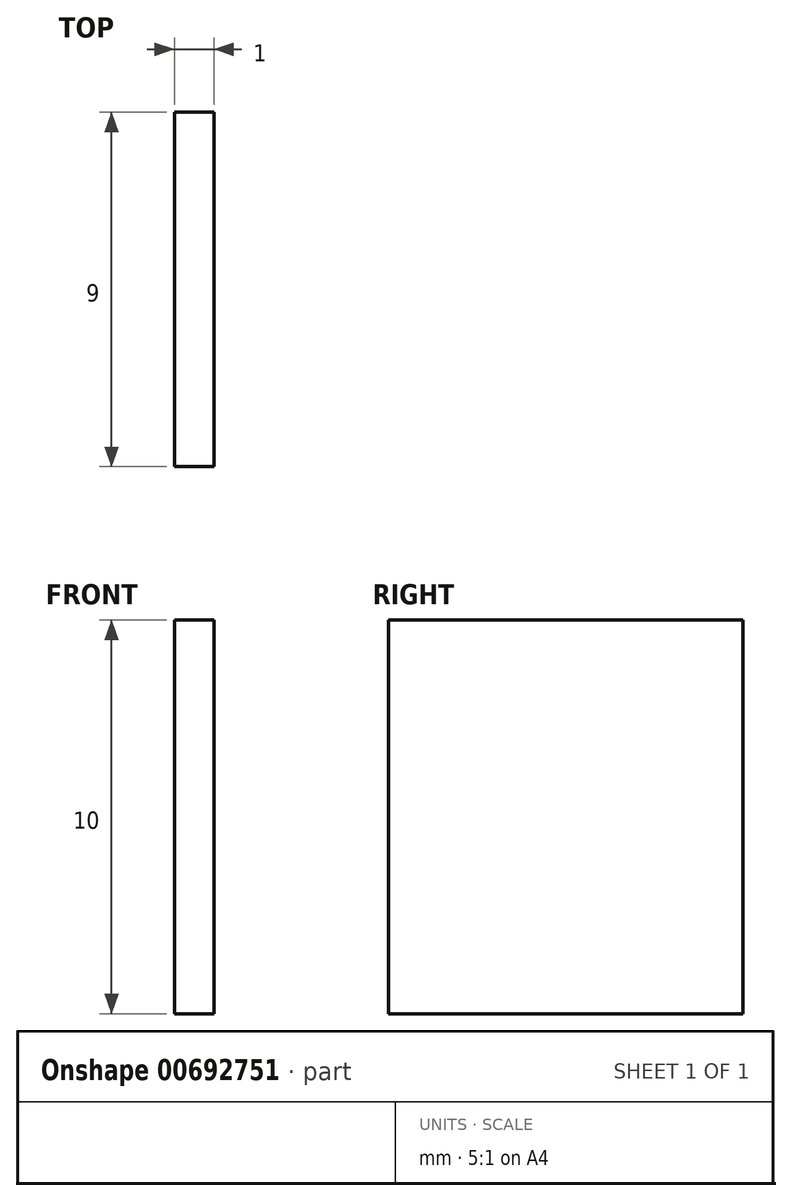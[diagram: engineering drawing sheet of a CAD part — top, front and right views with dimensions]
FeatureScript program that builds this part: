
annotation { "Feature Type Name" : "Feature", "Feature Type Description" : "" }
export const myFeature = defineFeature(function(context is Context, id is Id, definition is map)
    precondition{}
    {
        {
            var Q0;
            Q0=qCreatedBy(makeId("Right.planeOp"),FACE);
            var sketch = newSketch(context, id + "F0", { "sketchPlane" : qUnion([Q0])});
            skLineSegment(sketch, "E0.bottom", {"start": v(4.5, 5) * mm, "end": v(-4.5, 5) * mm});
            skLineSegment(sketch, "E0.top", {"start": v(4.5, -5) * mm, "end": v(-4.5, -5) * mm});
            skLineSegment(sketch, "E0.left", {"start": v(4.5, 5) * mm, "end": v(4.5, -5) * mm});
            skLineSegment(sketch, "E0.right", {"start": v(-4.5, 5) * mm, "end": v(-4.5, -5) * mm});
            skPoint(sketch, "E0.middle", {"position": v(0, 0) * mm});
            skSolve(sketch);
        }
        {
            var Q0;
            Q0=makeQuery(id+"F0.imprint","IMPRINT",FACE,{"disambiguationData":[TD([[makeQuery(id+"F0.imprint","IMPRINT",EDGE,{"derivedFrom":sQuery(id+"F0.wireOp",EDGE,"E0.bottom")}),1.0]])]});
            extrude(context, id + "F1", {"entities" : qUnion([Q0]), "depth" : 1 * mm, "offsetDistance" : 25 * mm});
        }
    });
